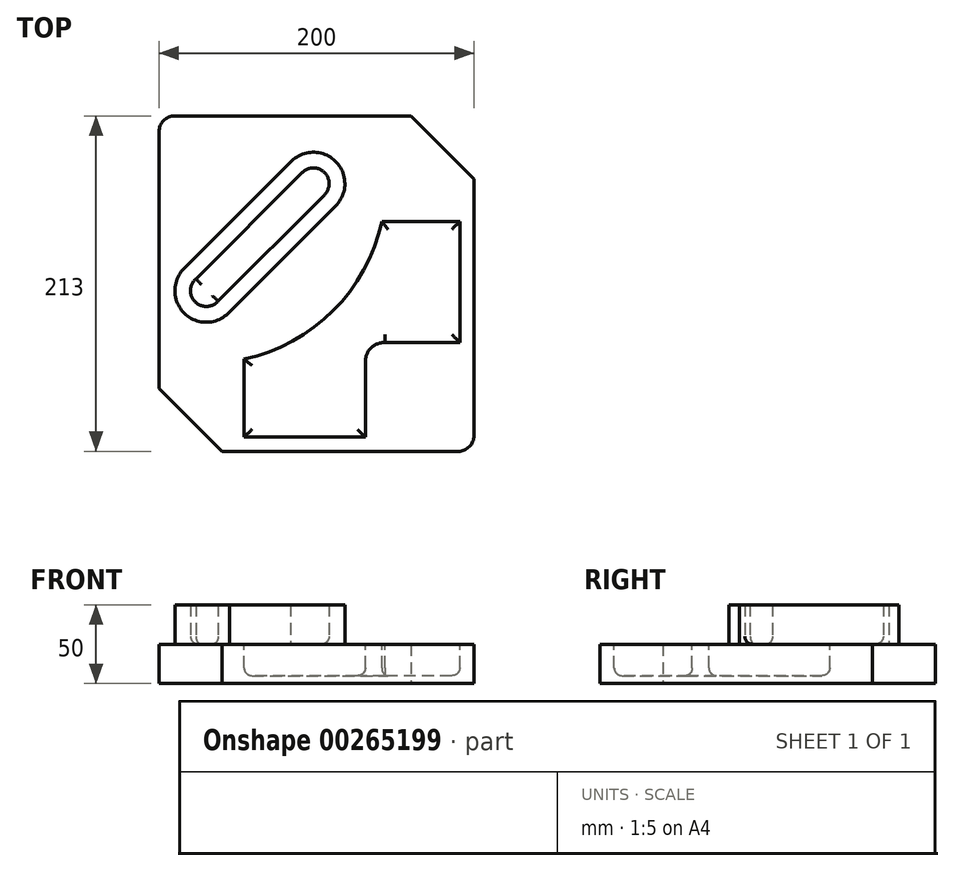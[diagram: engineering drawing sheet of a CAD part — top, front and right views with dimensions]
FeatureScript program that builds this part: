
annotation { "Feature Type Name" : "Feature", "Feature Type Description" : "" }
export const myFeature = defineFeature(function(context is Context, id is Id, definition is map)
    precondition{}
    {
        {
            var Q0;
            Q0=qCreatedBy(makeId("Top.planeOp"),FACE);
            var sketch = newSketch(context, id + "F0", { "sketchPlane" : qUnion([Q0])});
            skLineSegment(sketch, "E0", {"start": v(-74.3, 59.87) * mm, "end": v(75.7, 59.87) * mm});
            skLineSegment(sketch, "E1", {"start": v(115.7, 19.87) * mm, "end": v(115.7, -143.13) * mm});
            skLineSegment(sketch, "E2", {"start": v(105.7, -153.13) * mm, "end": v(-44.3, -153.13) * mm});
            skLineSegment(sketch, "E3", {"start": v(-84.3, -113.13) * mm, "end": v(-84.3, 49.87) * mm});
            skPoint(sketch, "E4.visualSharp", {"position": v(-84.3, 59.87) * mm});
            skArc(sketch, "E4.filletArc", {"start": v(-74.3, 59.87) * mm, "mid": v(-81.37, 56.94) * mm, "end": v(-84.3, 49.87) * mm});
            skPoint(sketch, "E5.visualSharp", {"position": v(115.7, -153.13) * mm});
            skArc(sketch, "E5.filletArc", {"start": v(105.7, -153.13) * mm, "mid": v(112.77, -150.2) * mm, "end": v(115.7, -143.13) * mm});
            skLineSegment(sketch, "E6", {"start": v(115.7, 19.87) * mm, "end": v(75.7, 59.87) * mm});
            skPoint(sketch, "E7.orphan", {"position": v(115.7, 59.87) * mm});
            skLineSegment(sketch, "E8", {"start": v(-44.3, -153.13) * mm, "end": v(-84.3, -113.13) * mm});
            skPoint(sketch, "E9.orphan", {"position": v(-84.3, -153.13) * mm});
            skSolve(sketch);
        }
        {
            var Q0;
            Q0=makeQuery(id+"F0.imprint","IMPRINT",FACE,{"disambiguationData":[TD([[makeQuery(id+"F0.imprint","IMPRINT",EDGE,{"derivedFrom":sQuery(id+"F0.wireOp",EDGE,"E0")}),-1.0]])]});
            extrude(context, id + "F1", {"entities" : qUnion([Q0]), "depth" : 25 * mm});
        }
        {
            var Q0;
            Q0=makeQuery(id+"F1.opExtrude","CAP_FACE",FACE,{"disambiguationData":[OSD([sQuery(id+"F0.wireOp",EDGE,"E0"),sQuery(id+"F0.wireOp",EDGE,"E1"),sQuery(id+"F0.wireOp",EDGE,"E2"),sQuery(id+"F0.wireOp",EDGE,"E3"),sQuery(id+"F0.wireOp",EDGE,"E4.filletArc"),sQuery(id+"F0.wireOp",EDGE,"E5.filletArc"),sQuery(id+"F0.wireOp",EDGE,"E6"),sQuery(id+"F0.wireOp",EDGE,"E8")])],"isStart":false});
            var sketch = newSketch(context, id + "F2", { "sketchPlane" : qUnion([Q0])});
            skArc(sketch, "E10", {"start": v(20.77, 9.8) * mm, "mid": v(20.77, 23.93) * mm, "end": v(6.63, 23.93) * mm});
            skArc(sketch, "E11", {"start": v(27.84, 2.72) * mm, "mid": v(27.6, 31.24) * mm, "end": v(-0.91, 30.52) * mm});
            skArc(sketch, "E12", {"start": v(-68.44, -37) * mm, "mid": v(-68.14, -65.57) * mm, "end": v(-39.58, -64.68) * mm});
            skArc(sketch, "E13", {"start": v(-60.85, -43.58) * mm, "mid": v(-61.37, -58.2) * mm, "end": v(-46.74, -57.68) * mm});
            skLineSegment(sketch, "E14", {"start": v(-0.91, 30.52) * mm, "end": v(-68.44, -37) * mm});
            skLineSegment(sketch, "E15", {"start": v(-39.58, -64.68) * mm, "end": v(27.84, 2.72) * mm});
            skLineSegment(sketch, "E16", {"start": v(-46.74, -57.68) * mm, "end": v(20.77, 9.8) * mm});
            skLineSegment(sketch, "E17", {"start": v(6.63, 23.93) * mm, "end": v(-60.85, -43.58) * mm});
            skSolve(sketch);
        }
        {
            var Q0;
            Q0=makeQuery(id+"F2.imprint","IMPRINT",FACE,{"disambiguationData":[TD([[makeQuery(id+"F2.imprint","IMPRINT",EDGE,{"derivedFrom":sQuery(id+"F2.wireOp",EDGE,"E10")}),-1.0]])]});
            extrude(context, id + "F3", {"entities" : qUnion([Q0]), "operationType" : NewBodyOperationType.ADD, "depth" : 25 * mm});
        }
        {
            var Q0;
            {var subQ0=sQuery(id+"F0.wireOp",EDGE,"E2");var subQ1=sQuery(id+"F0.wireOp",EDGE,"E8");var subQ2=sQuery(id+"F0.wireOp",EDGE,"E6");var subQ3=sQuery(id+"F0.wireOp",EDGE,"E5.filletArc");var subQ4=sQuery(id+"F0.wireOp",EDGE,"E4.filletArc");var subQ5=sQuery(id+"F0.wireOp",EDGE,"E0");var subQ6=sQuery(id+"F0.wireOp",EDGE,"E1");var subQ7=sQuery(id+"F0.wireOp",EDGE,"E3");Q0=makeQuery(id+"F3.boolean.opBoolean","SPLIT",FACE,{"disambiguationData":[TD([makeQuery(id+"F1.opExtrude","SWEPT_FACE",FACE,{"disambiguationData":[OSD([subQ5])]})])],"derivedFrom":makeQuery(id+"F1.opExtrude","CAP_FACE",FACE,{"disambiguationData":[OSD([subQ5,subQ6,subQ0,subQ7,subQ4,subQ3,subQ2,subQ1])],"isStart":false})});}
            var sketch = newSketch(context, id + "F4", { "sketchPlane" : qUnion([Q0])});
            skArc(sketch, "E18", {"start": v(-30.3, -94.58) * mm, "mid": v(26.31, -63.74) * mm, "end": v(57.15, -7.13) * mm});
            skLineSegment(sketch, "E19", {"start": v(106.7, -7.13) * mm, "end": v(57.15, -7.13) * mm});
            skLineSegment(sketch, "E20", {"start": v(106.7, -7.13) * mm, "end": v(106.7, -84.01) * mm});
            skLineSegment(sketch, "E21", {"start": v(106.7, -84.01) * mm, "end": v(58.44, -84.01) * mm});
            skArc(sketch, "E22", {"start": v(59.07, -84.01) * mm, "mid": v(50.39, -87.4) * mm, "end": v(46.76, -96) * mm});
            skLineSegment(sketch, "E23", {"start": v(46.7, -144.13) * mm, "end": v(-30.3, -144.06) * mm});
            skLineSegment(sketch, "E24", {"start": v(46.76, -96) * mm, "end": v(46.7, -144.13) * mm});
            skLineSegment(sketch, "E25", {"start": v(-30.3, -144.06) * mm, "end": v(-30.3, -94.58) * mm});
            skSolve(sketch);
        }
        {
            var Q0;
            Q0=makeQuery(id+"F4.imprint","IMPRINT",FACE,{"disambiguationData":[TD([[makeQuery(id+"F4.imprint","IMPRINT",EDGE,{"derivedFrom":sQuery(id+"F4.wireOp",EDGE,"E18")}),-1.0]])]});
            extrude(context, id + "F5", {"entities" : qUnion([Q0]), "operationType" : NewBodyOperationType.REMOVE, "oppositeDirection" : true, "depth" : 20 * mm});
        }
        {
            var Q0;
            Q0=makeQuery(id+"F5.boolean.opBoolean","COPY",EDGE,{"derivedFrom":makeQuery(id+"F5.opExtrude","CAP_EDGE",EDGE,{"disambiguationData":[OSD([sQuery(id+"F4.wireOp",EDGE,"E18")])],"isStart":true})});
            var Q1;
            Q1=makeQuery(id+"F5.boolean.opBoolean","COPY",EDGE,{"derivedFrom":makeQuery(id+"F5.opExtrude","CAP_EDGE",EDGE,{"disambiguationData":[OSD([sQuery(id+"F4.wireOp",EDGE,"E19")])],"isStart":true})});
            var Q2;
            Q2=makeQuery(id+"F5.boolean.opBoolean","COPY",EDGE,{"derivedFrom":makeQuery(id+"F5.opExtrude","CAP_EDGE",EDGE,{"disambiguationData":[OSD([sQuery(id+"F4.wireOp",EDGE,"E20")])],"isStart":true})});
            var Q3;
            Q3=makeQuery(id+"F5.boolean.opBoolean","COPY",EDGE,{"derivedFrom":makeQuery(id+"F5.opExtrude","CAP_EDGE",EDGE,{"disambiguationData":[OSD([sQuery(id+"F4.wireOp",EDGE,"E21")])],"isStart":true})});
            var Q4;
            Q4=makeQuery(id+"F5.boolean.opBoolean","COPY",EDGE,{"derivedFrom":makeQuery(id+"F5.opExtrude","CAP_EDGE",EDGE,{"disambiguationData":[OSD([sQuery(id+"F4.wireOp",EDGE,"E22")])],"isStart":true})});
            var Q5;
            Q5=makeQuery(id+"F5.boolean.opBoolean","COPY",EDGE,{"derivedFrom":makeQuery(id+"F5.opExtrude","CAP_EDGE",EDGE,{"disambiguationData":[OSD([sQuery(id+"F4.wireOp",EDGE,"E23")])],"isStart":true})});
            var Q6;
            Q6=makeQuery(id+"F5.boolean.opBoolean","COPY",EDGE,{"derivedFrom":makeQuery(id+"F5.opExtrude","CAP_EDGE",EDGE,{"disambiguationData":[OSD([sQuery(id+"F4.wireOp",EDGE,"E25")])],"isStart":true})});
            var Q7;
            Q7=makeQuery(id+"F3.opExtrude","CAP_EDGE",EDGE,{"disambiguationData":[OSD([sQuery(id+"F2.wireOp",EDGE,"E15")])],"isStart":true});
            var Q8;
            Q8=makeQuery(id+"F3.opExtrude","CAP_EDGE",EDGE,{"disambiguationData":[OSD([sQuery(id+"F2.wireOp",EDGE,"E12")])],"isStart":true});
            var Q9;
            Q9=makeQuery(id+"F5.boolean.opBoolean","COPY",EDGE,{"derivedFrom":makeQuery(id+"F5.opExtrude","CAP_EDGE",EDGE,{"disambiguationData":[OSD([sQuery(id+"F4.wireOp",EDGE,"E18")])],"isStart":false})});
            var Q10;
            Q10=makeQuery(id+"F5.boolean.opBoolean","COPY",EDGE,{"derivedFrom":makeQuery(id+"F5.opExtrude","CAP_EDGE",EDGE,{"disambiguationData":[OSD([sQuery(id+"F4.wireOp",EDGE,"E19")])],"isStart":false})});
            var Q11;
            Q11=makeQuery(id+"F5.boolean.opBoolean","COPY",EDGE,{"derivedFrom":makeQuery(id+"F5.opExtrude","CAP_EDGE",EDGE,{"disambiguationData":[OSD([sQuery(id+"F4.wireOp",EDGE,"E20")])],"isStart":false})});
            var Q12;
            Q12=makeQuery(id+"F5.boolean.opBoolean","COPY",EDGE,{"derivedFrom":makeQuery(id+"F5.opExtrude","CAP_EDGE",EDGE,{"disambiguationData":[OSD([sQuery(id+"F4.wireOp",EDGE,"E24")])],"isStart":false})});
            var Q13;
            Q13=makeQuery(id+"F5.boolean.opBoolean","COPY",EDGE,{"derivedFrom":makeQuery(id+"F5.opExtrude","CAP_EDGE",EDGE,{"disambiguationData":[OSD([sQuery(id+"F4.wireOp",EDGE,"E21")])],"isStart":false})});
            var Q14;
            Q14=makeQuery(id+"F5.boolean.opBoolean","COPY",EDGE,{"derivedFrom":makeQuery(id+"F5.opExtrude","CAP_EDGE",EDGE,{"disambiguationData":[OSD([sQuery(id+"F4.wireOp",EDGE,"E23")])],"isStart":false})});
            var Q15;
            Q15=makeQuery(id+"F5.boolean.opBoolean","COPY",EDGE,{"derivedFrom":makeQuery(id+"F5.opExtrude","CAP_EDGE",EDGE,{"disambiguationData":[OSD([sQuery(id+"F4.wireOp",EDGE,"E25")])],"isStart":false})});
            var Q16;
            Q16=makeQuery(id+"F3.opExtrude","CAP_EDGE",EDGE,{"disambiguationData":[OSD([sQuery(id+"F2.wireOp",EDGE,"E17")])],"isStart":true});
            var Q17;
            Q17=makeQuery(id+"F3.opExtrude","CAP_EDGE",EDGE,{"disambiguationData":[OSD([sQuery(id+"F2.wireOp",EDGE,"E10")])],"isStart":true});
            var Q18;
            Q18=makeQuery(id+"F3.opExtrude","CAP_EDGE",EDGE,{"disambiguationData":[OSD([sQuery(id+"F2.wireOp",EDGE,"E13")])],"isStart":true});
            fillet(context, id + "F6", {"entities" : qUnion([Q0, Q1, Q2, Q3, Q4, Q5, Q6, Q7, Q8, Q9, Q10, Q11, Q12, Q13, Q14, Q15, Q16, Q17, Q18]), "radius" : 5 * mm, "tangentPropagation" : true, "allowEdgeOverflow" : false});
        }
    });
